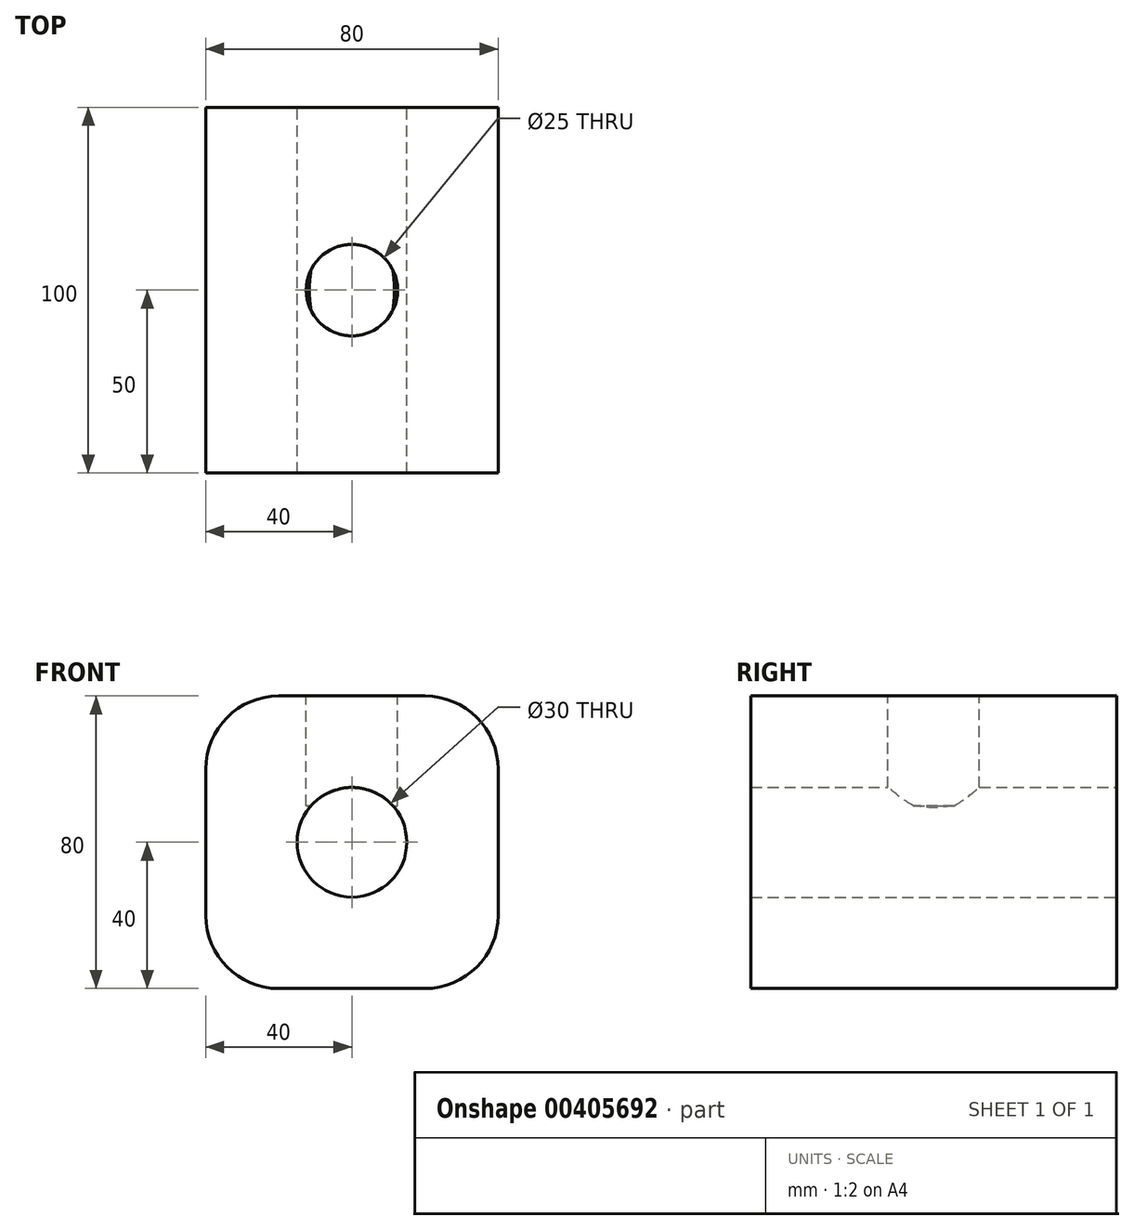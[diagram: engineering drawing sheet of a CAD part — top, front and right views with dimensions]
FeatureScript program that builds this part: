
annotation { "Feature Type Name" : "Feature", "Feature Type Description" : "" }
export const myFeature = defineFeature(function(context is Context, id is Id, definition is map)
    precondition{}
    {
        {
            var Q0;
            Q0=qCreatedBy(makeId("Front.planeOp"),FACE);
            var sketch = newSketch(context, id + "F0", { "sketchPlane" : qUnion([Q0])});
            skLineSegment(sketch, "E0.bottom", {"start": v(-20, 40) * mm, "end": v(20, 40) * mm});
            skLineSegment(sketch, "E0.top", {"start": v(-20, -40) * mm, "end": v(20, -40) * mm});
            skLineSegment(sketch, "E0.left", {"start": v(-40, 20) * mm, "end": v(-40, -20) * mm});
            skLineSegment(sketch, "E0.right", {"start": v(40, 20) * mm, "end": v(40, -20) * mm});
            skPoint(sketch, "E0.middle", {"position": v(0, 0) * mm});
            skPoint(sketch, "E1.visualSharp", {"position": v(-40, 40) * mm});
            skArc(sketch, "E1.filletArc", {"start": v(-20, 40) * mm, "mid": v(-34.14, 34.14) * mm, "end": v(-40, 20) * mm});
            skPoint(sketch, "E2.visualSharp", {"position": v(40, 40) * mm});
            skArc(sketch, "E2.filletArc", {"start": v(40, 20) * mm, "mid": v(34.14, 34.14) * mm, "end": v(20, 40) * mm});
            skPoint(sketch, "E3.visualSharp", {"position": v(40, -40) * mm});
            skArc(sketch, "E3.filletArc", {"start": v(20, -40) * mm, "mid": v(34.14, -34.14) * mm, "end": v(40, -20) * mm});
            skPoint(sketch, "E4.visualSharp", {"position": v(-40, -40) * mm});
            skArc(sketch, "E4.filletArc", {"start": v(-40, -20) * mm, "mid": v(-34.14, -34.14) * mm, "end": v(-20, -40) * mm});
            skCircle(sketch, "E5", {"center": v(0, 0) * mm, "radius": 15 * mm});
            skSolve(sketch);
        }
        {
            var Q0;
            Q0=makeQuery(id+"F0.imprint","IMPRINT",FACE,{"disambiguationData":[TD([[makeQuery(id+"F0.imprint","IMPRINT",EDGE,{"derivedFrom":sQuery(id+"F0.wireOp",EDGE,"E0.bottom")}),-1.0]])]});
            extrude(context, id + "F1", {"entities" : qUnion([Q0]), "depth" : 50 * mm, "hasSecondDirection" : true, "secondDirectionOppositeDirection" : true, "secondDirectionDepth" : 50 * mm});
        }
        {
            var Q0;
            Q0=makeQuery(id+"F1.opExtrude","SWEPT_FACE",FACE,{"disambiguationData":[OSD([sQuery(id+"F0.wireOp",EDGE,"E0.bottom")])]});
            var sketch = newSketch(context, id + "F2", { "sketchPlane" : qUnion([Q0])});
            skCircle(sketch, "E6", {"center": v(0, 0) * mm, "radius": 12.5 * mm});
            skSolve(sketch);
        }
        {
            var Q0;
            Q0=sQuery(id+"F2.wireOp",VERTEX,"E6.center");
            var Q1;
            Q1=makeQuery(id+"F1.opExtrude","SWEPT_BODY",BODY,{"disambiguationData":[OSD([sQuery(id+"F0.wireOp",EDGE,"E0.bottom"),sQuery(id+"F0.wireOp",EDGE,"E0.top"),sQuery(id+"F0.wireOp",EDGE,"E0.left"),sQuery(id+"F0.wireOp",EDGE,"E0.right"),sQuery(id+"F0.wireOp",EDGE,"E1.filletArc"),sQuery(id+"F0.wireOp",EDGE,"E2.filletArc"),sQuery(id+"F0.wireOp",EDGE,"E3.filletArc"),sQuery(id+"F0.wireOp",EDGE,"E4.filletArc"),sQuery(id+"F0.wireOp",EDGE,"E5")])]});
            hole(context, id + "F3", {"style" : HoleStyle.SIMPLE, "endStyle" : HoleEndStyle.BLIND, "holeDiameter" : 25 * mm, "holeDepth" : 30 * mm, "isTappedThrough" : true, "tappedDepth" : 12 * mm, "tapClearance" : 3, "locations" : qUnion([Q0]), "scope" : qUnion([Q1])});
        }
    });
